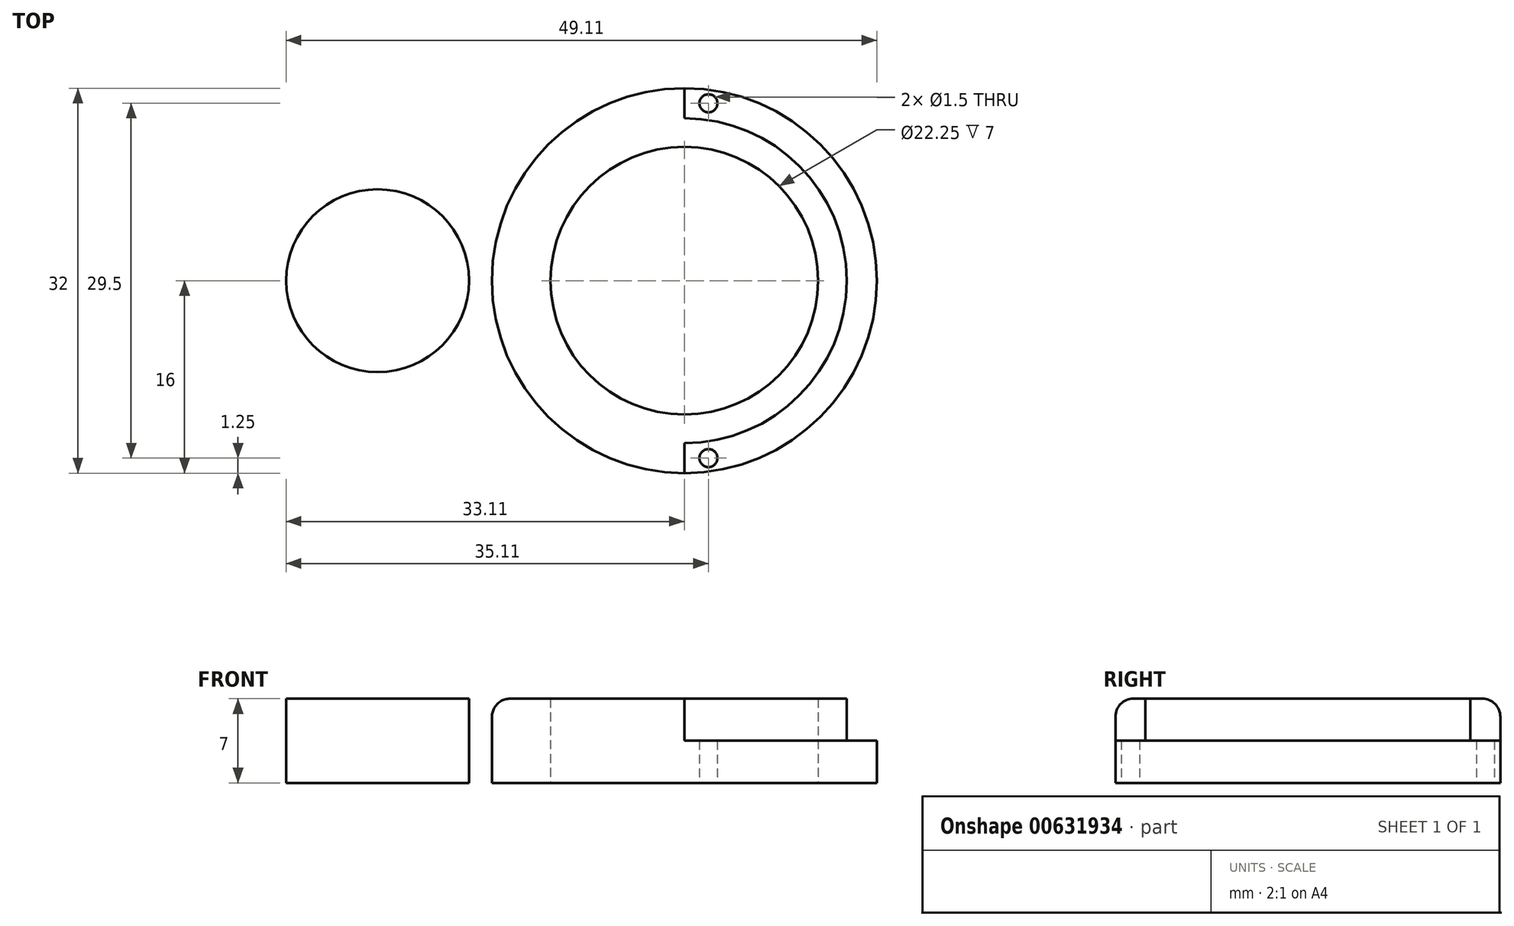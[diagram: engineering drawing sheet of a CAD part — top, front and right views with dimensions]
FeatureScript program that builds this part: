
annotation { "Feature Type Name" : "Feature", "Feature Type Description" : "" }
export const myFeature = defineFeature(function(context is Context, id is Id, definition is map)
    precondition{}
    {
        {
            var Q0;
            Q0=qCreatedBy(makeId("Top.planeOp"),FACE);
            var sketch = newSketch(context, id + "F0", { "sketchPlane" : qUnion([Q0])});
            skCircle(sketch, "E0", {"center": v(0, 0) * mm, "radius": 11.12 * mm});
            skCircle(sketch, "E1", {"center": v(0, 0) * mm, "radius": 16 * mm});
            skLineSegment(sketch, "E2", {"start": v(0, 0) * mm, "end": v(34.83, 0) * mm, "construction": true});
            skCircle(sketch, "E3", {"center": v(25.5, 0) * mm, "radius": 7.6 * mm});
            skArc(sketch, "E4", {"start": v(20.04, -10.68) * mm, "mid": v(37.5, 0) * mm, "end": v(20.04, 10.68) * mm});
            skArc(sketch, "E5", {"start": v(23.21, -11.78) * mm, "mid": v(17.1, -10.35) * mm, "end": v(10.96, -11.66) * mm});
            skArc(sketch, "E6.MirrorCS", {"start": v(23.21, 11.78) * mm, "mid": v(17.1, 10.35) * mm, "end": v(10.96, 11.66) * mm});
            skLineSegment(sketch, "E7.MirrorCS", {"start": v(0, 0) * mm, "end": v(-34.83, 0) * mm, "construction": true});
            skCircle(sketch, "E8.MirrorC", {"center": v(-25.5, 0) * mm, "radius": 7.6 * mm});
            skArc(sketch, "E9.MirrorC", {"start": v(-20.04, -10.68) * mm, "mid": v(-37.5, 0) * mm, "end": v(-20.04, 10.68) * mm});
            skArc(sketch, "E10.MirrorCS", {"start": v(-23.21, -11.78) * mm, "mid": v(-17.1, -10.35) * mm, "end": v(-10.96, -11.66) * mm});
            skArc(sketch, "E11.MirrorCS", {"start": v(-23.21, 11.78) * mm, "mid": v(-17.1, 10.35) * mm, "end": v(-10.96, 11.66) * mm});
            skLineSegment(sketch, "E12", {"start": v(0, -16) * mm, "end": v(0, -13.5) * mm});
            skLineSegment(sketch, "E13", {"start": v(0, 16) * mm, "end": v(0, 13.5) * mm});
            skArc(sketch, "E14", {"start": v(0, -13.5) * mm, "mid": v(13.5, 0) * mm, "end": v(0, 13.5) * mm});
            skCircle(sketch, "E15", {"center": v(2, 14.75) * mm, "radius": 0.75 * mm});
            skPoint(sketch, "E16.endSnap0", {"position": v(0, -14.75) * mm});
            skCircle(sketch, "E17", {"center": v(2, -14.75) * mm, "radius": 0.75 * mm});
            skSolve(sketch);
        }
        {
            var Q0;
            Q0=makeQuery(id+"F0.imprint","IMPRINT",FACE,{"disambiguationData":[TD([[makeQuery(id+"F0.imprint","IMPRINT",EDGE,{"derivedFrom":sQuery(id+"F0.wireOp",EDGE,"E0")}),-1.0]])]});
            var Q1;
            Q1=makeQuery(id+"F0.imprint","IMPRINT",FACE,{"disambiguationData":[TD([[makeQuery(id+"F0.imprint","IMPRINT",EDGE,{"derivedFrom":sQuery(id+"F0.wireOp",EDGE,"E8.MirrorC")}),1.0]])]});
            extrude(context, id + "F1", {"entities" : qUnion([Q0, Q1]), "depth" : 7 * mm, "offsetDistance" : 25 * mm});
        }
        {
            var Q0;
            {var subQ0=sQuery(id+"F0.wireOp",EDGE,"E12");Q0=makeQuery(id+"F0.imprint","IMPRINT",FACE,{"disambiguationData":[TD([[makeQuery(id+"F0.imprint","IMPRINT",EDGE,{"derivedFrom":subQ0}),-1.0]])]});}
            extrude(context, id + "F2", {"entities" : qUnion([Q0]), "operationType" : NewBodyOperationType.ADD, "depth" : 3.5 * mm, "offsetDistance" : 25 * mm});
        }
        {
            var Q0;
            {var subQ0=sQuery(id+"F0.wireOp",EDGE,"E1");Q0=makeQuery(id+"F1.opExtrude","CAP_EDGE",EDGE,{"disambiguationData":[OSD([subQ0]),TDD([makeQuery(id+"F0.imprint","IMPRINT",EDGE,{"disambiguationData":[TD([[makeQuery(id+"F0.imprint","INTERSECT",VERTEX,{"derivedFrom":[subQ0,sQuery(id+"F0.wireOp",EDGE,"E11.MirrorCS")]}),1.0]])],"derivedFrom":subQ0})])],"isStart":false});}
            var Q1;
            Q1=makeQuery(id+"F1.opExtrude","CAP_EDGE",EDGE,{"disambiguationData":[OSD([sQuery(id+"F0.wireOp",EDGE,"E11.MirrorCS")])],"isStart":false});
            var Q2;
            Q2=makeQuery(id+"F1.opExtrude","CAP_EDGE",EDGE,{"disambiguationData":[OSD([sQuery(id+"F0.wireOp",EDGE,"E9.MirrorC")])],"isStart":false});
            var Q3;
            Q3=makeQuery(id+"F1.opExtrude","CAP_EDGE",EDGE,{"disambiguationData":[OSD([sQuery(id+"F0.wireOp",EDGE,"E10.MirrorCS")])],"isStart":false});
            var Q4;
            {var subQ0=sQuery(id+"F0.wireOp",EDGE,"E1");Q4=makeQuery(id+"F1.opExtrude","CAP_EDGE",EDGE,{"disambiguationData":[OSD([subQ0]),TDD([makeQuery(id+"F0.imprint","IMPRINT",EDGE,{"disambiguationData":[TD([[makeQuery(id+"F0.imprint","INTERSECT",VERTEX,{"derivedFrom":[subQ0,sQuery(id+"F0.wireOp",EDGE,"E10.MirrorCS")]}),-1.0]])],"derivedFrom":subQ0})])],"isStart":false});}
            fillet(context, id + "F3", {"entities" : qUnion([Q0, Q1, Q2, Q3, Q4]), "radius" : 1.5 * mm, "tangentPropagation" : true, "allowEdgeOverflow" : false});
        }
    });
